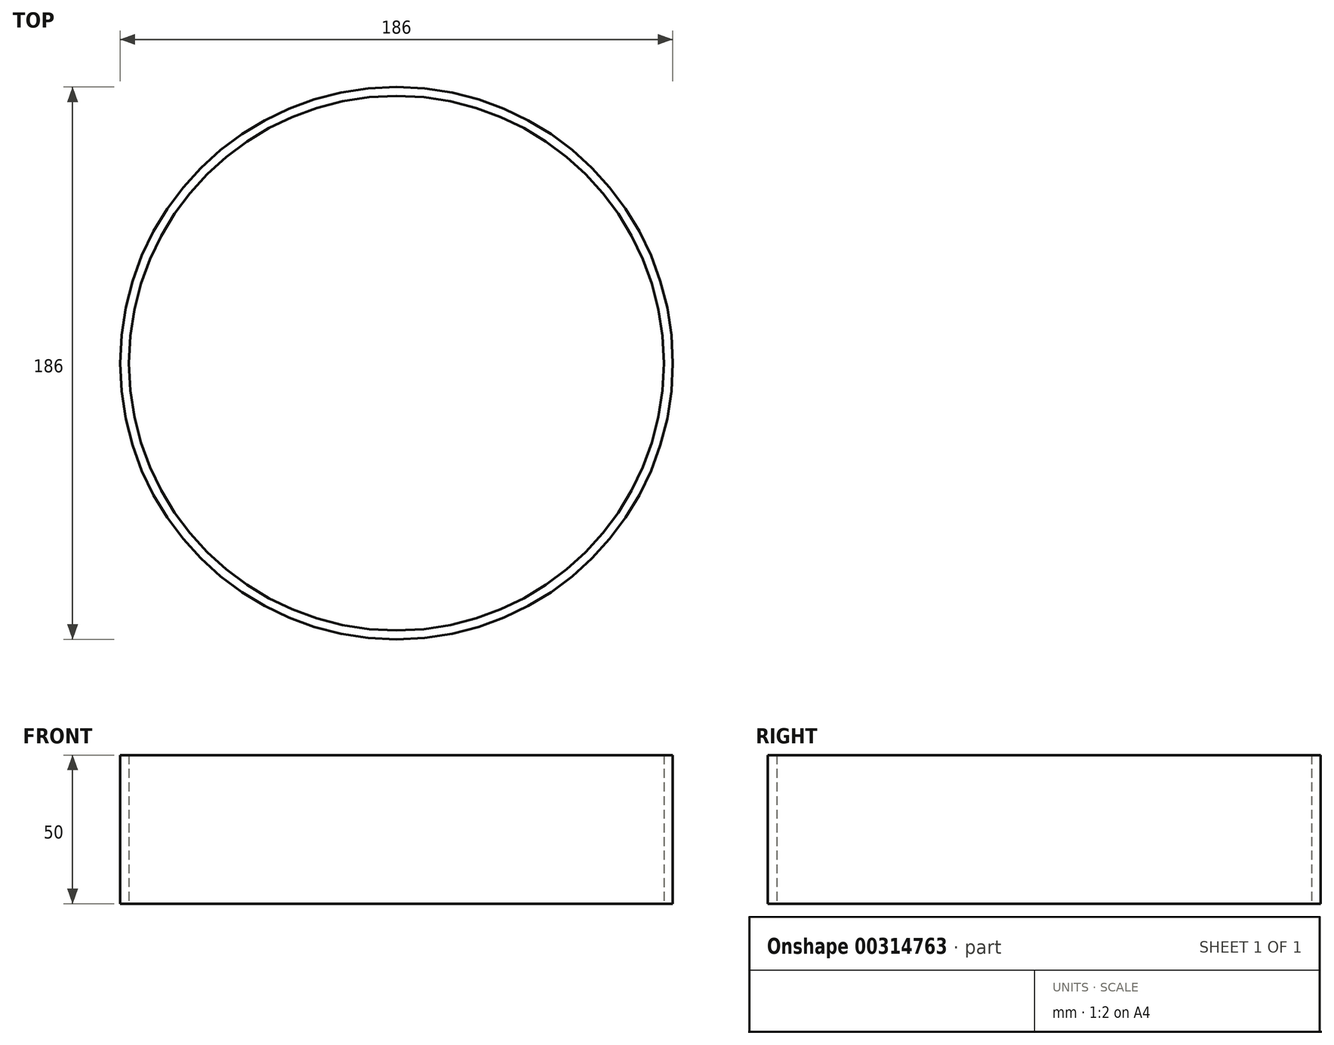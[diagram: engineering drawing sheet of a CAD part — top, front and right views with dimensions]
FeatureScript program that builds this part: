
annotation { "Feature Type Name" : "Feature", "Feature Type Description" : "" }
export const myFeature = defineFeature(function(context is Context, id is Id, definition is map)
    precondition{}
    {
        {
            var Q0;
            Q0=qCreatedBy(makeId("Top.planeOp"),FACE);
            var sketch = newSketch(context, id + "F0", { "sketchPlane" : qUnion([Q0])});
            skCircle(sketch, "E0", {"center": v(0, 0) * mm, "radius": 93 * mm});
            skCircle(sketch, "E1", {"center": v(0, 0) * mm, "radius": 90 * mm});
            skSolve(sketch);
        }
        {
            var Q0;
            Q0 = qSketchRegion(id + "F0", true);
            extrude(context, id + "F1", {"entities" : qUnion([Q0]), "depth" : 50 * mm, "offsetDistance" : 25 * mm});
        }
    });
